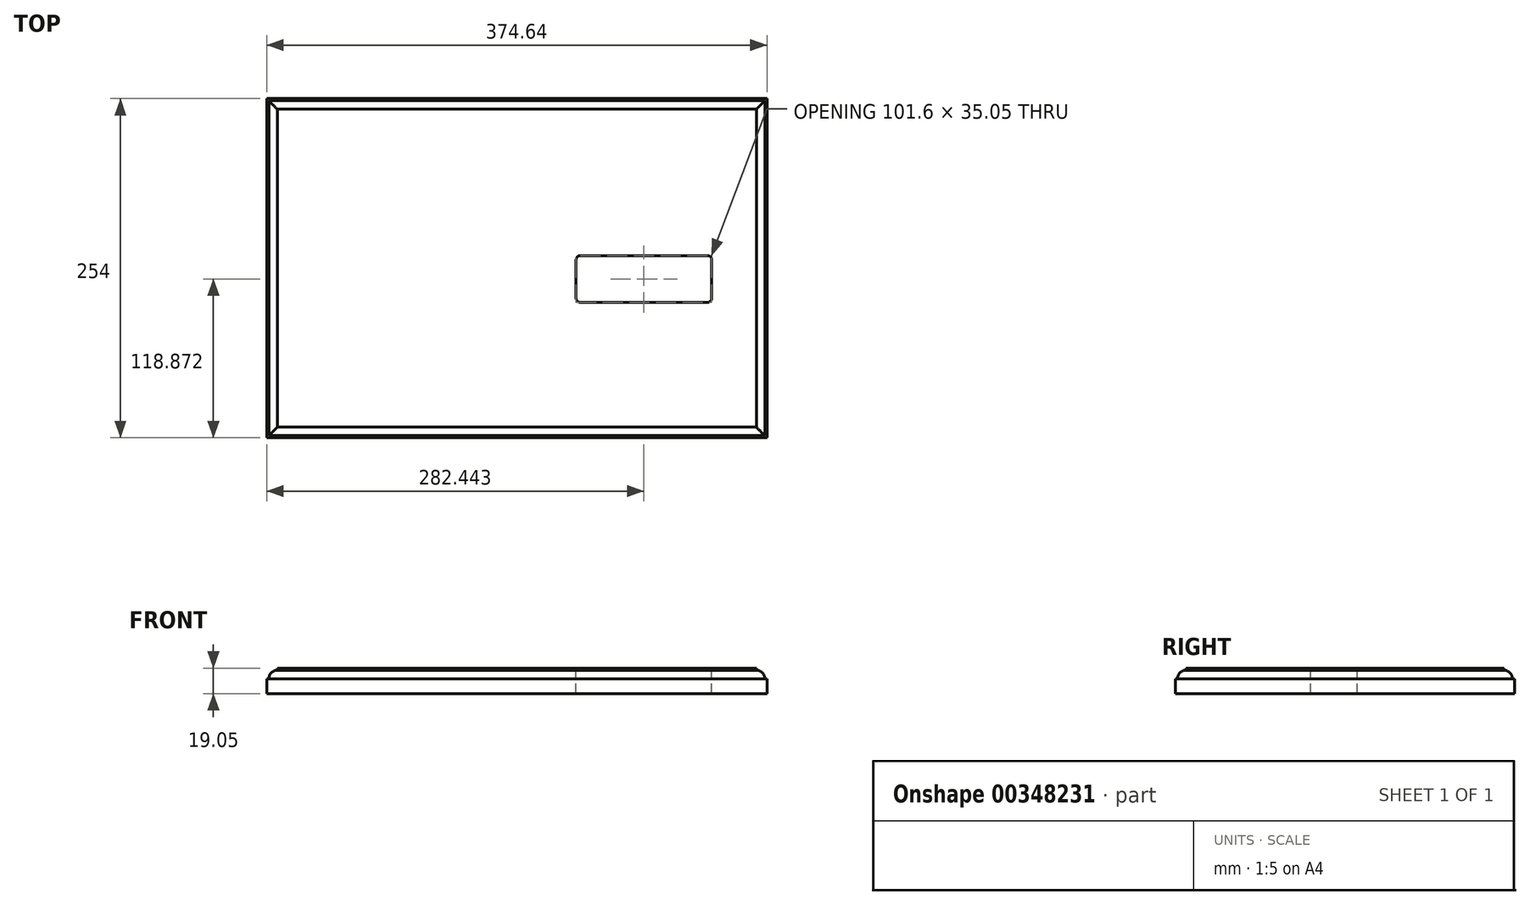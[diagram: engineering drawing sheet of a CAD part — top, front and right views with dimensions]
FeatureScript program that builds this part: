
annotation { "Feature Type Name" : "Feature", "Feature Type Description" : "" }
export const myFeature = defineFeature(function(context is Context, id is Id, definition is map)
    precondition{}
    {
        {
            var Q0;
            Q0=qCreatedBy(makeId("Top.planeOp"),FACE);
            var sketch = newSketch(context, id + "F0", { "sketchPlane" : qUnion([Q0])});
            skLineSegment(sketch, "E0.rect.bottom", {"start": v(187.33, -127) * mm, "end": v(-187.33, -127) * mm});
            skLineSegment(sketch, "E0.rect.top", {"start": v(187.33, 127) * mm, "end": v(-187.33, 127) * mm});
            skLineSegment(sketch, "E0.rect.left", {"start": v(187.33, -127) * mm, "end": v(187.33, 127) * mm});
            skLineSegment(sketch, "E0.rect.right", {"start": v(-187.33, -127) * mm, "end": v(-187.33, 127) * mm});
            skPoint(sketch, "E0.rect.middle", {"position": v(0, 0) * mm});
            skLineSegment(sketch, "E1.rect.bottom", {"start": v(142.75, 9.4) * mm, "end": v(47.5, 9.4) * mm});
            skLineSegment(sketch, "E1.rect.top", {"start": v(142.75, -25.65) * mm, "end": v(47.5, -25.65) * mm});
            skLineSegment(sketch, "E1.rect.left", {"start": v(145.92, 6.22) * mm, "end": v(145.92, -22.48) * mm});
            skLineSegment(sketch, "E1.rect.right", {"start": v(44.32, 6.22) * mm, "end": v(44.32, -22.48) * mm});
            skPoint(sketch, "E1.rect.middle", {"position": v(95.12, -8.13) * mm});
            skPoint(sketch, "E2.visualSharp", {"position": v(44.32, 9.4) * mm});
            skArc(sketch, "E2.filletArc", {"start": v(47.5, 9.4) * mm, "mid": v(45.25, 8.47) * mm, "end": v(44.32, 6.22) * mm});
            skPoint(sketch, "E3.visualSharp", {"position": v(145.92, 9.4) * mm});
            skArc(sketch, "E3.filletArc", {"start": v(145.92, 6.22) * mm, "mid": v(145, 8.47) * mm, "end": v(142.75, 9.4) * mm});
            skPoint(sketch, "E4.visualSharp", {"position": v(145.92, -25.65) * mm});
            skArc(sketch, "E4.filletArc", {"start": v(142.75, -25.65) * mm, "mid": v(145, -24.72) * mm, "end": v(145.92, -22.48) * mm});
            skPoint(sketch, "E5.visualSharp", {"position": v(44.32, -25.65) * mm});
            skArc(sketch, "E5.filletArc", {"start": v(44.32, -22.48) * mm, "mid": v(45.25, -24.72) * mm, "end": v(47.5, -25.65) * mm});
            skSolve(sketch);
        }
        {
            var Q0;
            Q0=qSketchRegion(id+"F0",true);
            extrude(context, id + "F1", {"entities" : qUnion([Q0]), "oppositeDirection" : true, "depth" : 19.05 * mm});
        }
        {
            var Q0;
            Q0=qCreatedBy(makeId("Front.planeOp"),FACE);
            var sketch = newSketch(context, id + "F2", { "sketchPlane" : qUnion([Q0])});
            skLineSegment(sketch, "E6", {"start": v(179.37, 0) * mm, "end": v(179.37, -1.6) * mm});
            skLineSegment(sketch, "E7", {"start": v(187.33, -7.95) * mm, "end": v(185.72, -7.95) * mm});
            skArc(sketch, "E8", {"start": v(185.72, -7.95) * mm, "mid": v(183.86, -3.46) * mm, "end": v(179.37, -1.6) * mm});
            skLineSegment(sketch, "E9", {"start": v(179.37, 0) * mm, "end": v(187.33, 0) * mm});
            skLineSegment(sketch, "E10", {"start": v(187.33, 0) * mm, "end": v(187.33, -7.95) * mm});
            skLineSegment(sketch, "E11.MirrorCS", {"start": v(-179.37, 0) * mm, "end": v(-179.37, -1.6) * mm});
            skLineSegment(sketch, "E12.MirrorCS", {"start": v(-187.33, -7.95) * mm, "end": v(-185.72, -7.95) * mm});
            skArc(sketch, "E13.MirrorCS", {"start": v(-185.72, -7.95) * mm, "mid": v(-183.86, -3.46) * mm, "end": v(-179.37, -1.6) * mm});
            skLineSegment(sketch, "E14.MirrorCS", {"start": v(-179.37, 0) * mm, "end": v(-187.33, 0) * mm});
            skLineSegment(sketch, "E15.MirrorCS", {"start": v(-187.33, 0) * mm, "end": v(-187.33, -7.95) * mm});
            skSolve(sketch);
        }
        {
            var Q0;
            Q0=qSketchRegion(id+"F2",true);
            extrude(context, id + "F3", {"entities" : qUnion([Q0]), "operationType" : NewBodyOperationType.REMOVE, "endBound" : BoundingType.SYMMETRIC, "oppositeDirection" : true, "depth" : 304.8 * mm});
        }
        {
            var Q0;
            Q0=qCreatedBy(makeId("Right.planeOp"),FACE);
            var sketch = newSketch(context, id + "F4", { "sketchPlane" : qUnion([Q0])});
            skLineSegment(sketch, "E16", {"start": v(119.05, 0) * mm, "end": v(119.05, -1.6) * mm});
            skLineSegment(sketch, "E17", {"start": v(127, -7.95) * mm, "end": v(125.4, -7.95) * mm});
            skArc(sketch, "E18", {"start": v(125.4, -7.95) * mm, "mid": v(123.54, -3.46) * mm, "end": v(119.05, -1.6) * mm});
            skLineSegment(sketch, "E19", {"start": v(119.05, 0) * mm, "end": v(127, 0) * mm});
            skLineSegment(sketch, "E20", {"start": v(127, 0) * mm, "end": v(127, -7.95) * mm});
            skLineSegment(sketch, "E21.MirrorCS", {"start": v(-119.05, 0) * mm, "end": v(-119.05, -1.6) * mm});
            skArc(sketch, "E22.MirrorCS", {"start": v(-125.4, -7.95) * mm, "mid": v(-123.54, -3.46) * mm, "end": v(-119.05, -1.6) * mm});
            skLineSegment(sketch, "E23.MirrorCS", {"start": v(-127, -7.95) * mm, "end": v(-125.4, -7.95) * mm});
            skLineSegment(sketch, "E24.MirrorCS", {"start": v(-119.05, 0) * mm, "end": v(-127, 0) * mm});
            skLineSegment(sketch, "E25.MirrorCS", {"start": v(-127, 0) * mm, "end": v(-127, -7.95) * mm});
            skSolve(sketch);
        }
        {
            var Q0;
            Q0=qSketchRegion(id+"F4",true);
            extrude(context, id + "F5", {"entities" : qUnion([Q0]), "operationType" : NewBodyOperationType.REMOVE, "endBound" : BoundingType.SYMMETRIC, "oppositeDirection" : true, "depth" : 406.4 * mm});
        }
    });
